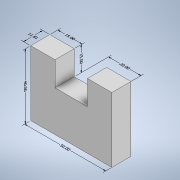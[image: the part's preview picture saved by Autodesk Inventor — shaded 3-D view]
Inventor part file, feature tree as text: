
AUTODESK INVENTOR PART (.ipt)
format: ipt  version: 2021 (Build 250183000, 183)  size: 112,128 bytes
history: native  units: in
note: dims shown in document units (in); Inventor stores cm internally (conversion verified against a paired STEP export)
features: other x7, extrude x1, sketch x1
ambient origin geometry x8: Origin, YZ Plane, XZ Plane, XY Plane, X Axis, Y Axis, Z Axis, Center Point
bodies: Solid1 (feature_tree)
feature tree (9):
  other  "Annotations"
  extrude  "Extrusion1"  Depth=40.0in
  sketch  "Sketch1"  dims[d0=50.0in d1=40.0in d6=11.811in d7=0.0in d10=40.0in d11=0.0in d12=0.3937in d13=50.0in d14=0.0in d15=0.3937in d16=15.0in d17=0.0in d18=0.3937in d19=20.0in d20=0.0in d21=0.3937in d22=15.0in d23=0.0in d24=0.3937in d25=11.811in d8=0.0in d9=0.3937in]
  other  "Linear Dimension 1"
  other  "Linear Dimension 2"
  other  "Linear Dimension 3"
  other  "Linear Dimension 4"
  other  "Linear Dimension 5"
  other  "Linear Dimension 6"
